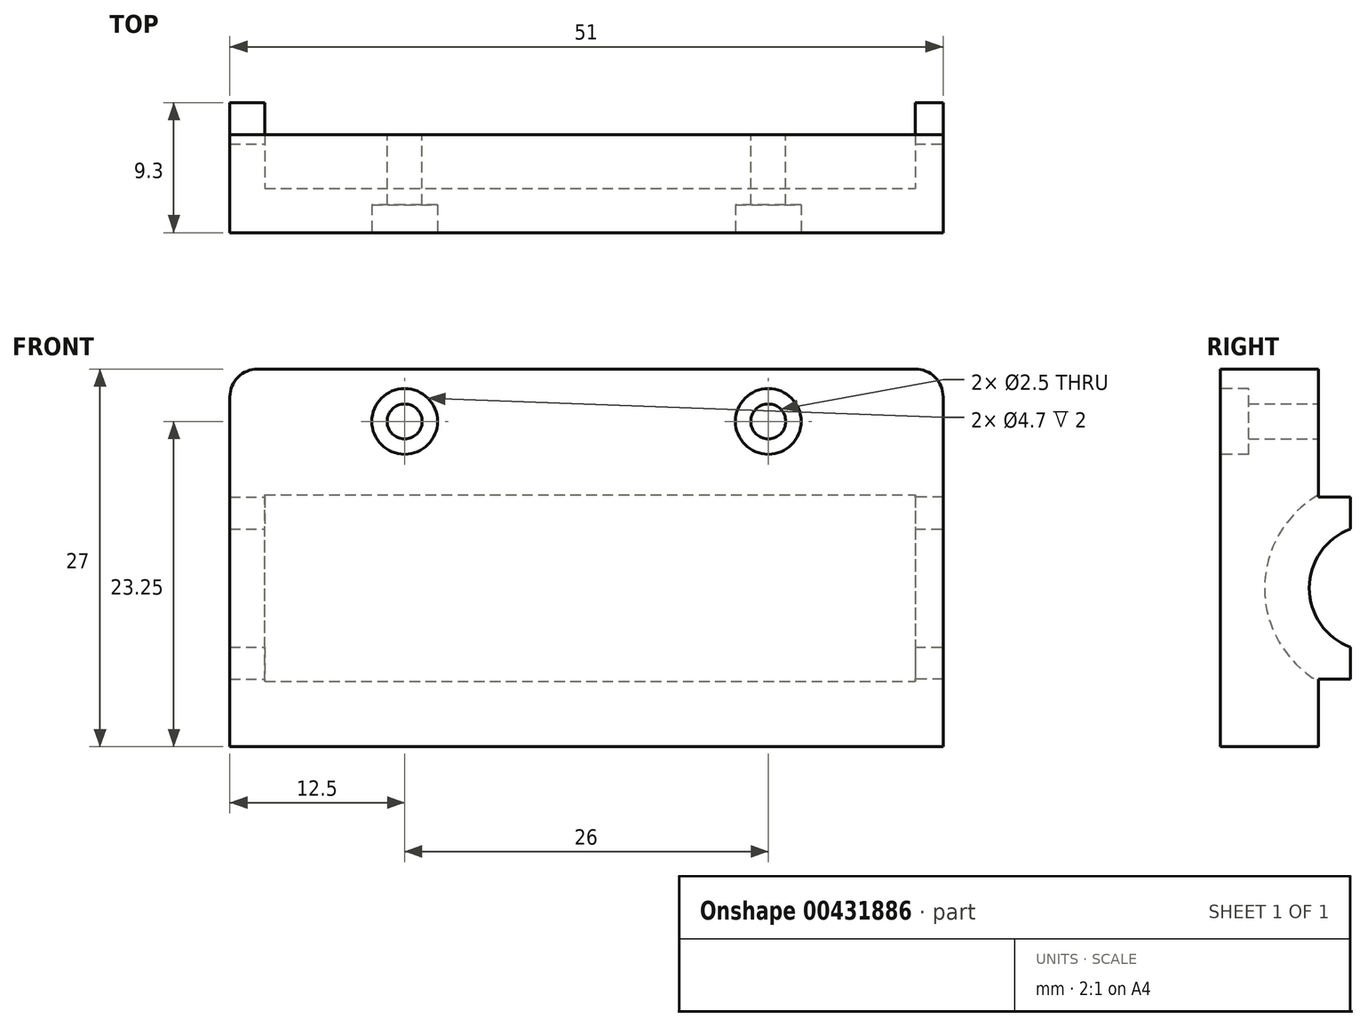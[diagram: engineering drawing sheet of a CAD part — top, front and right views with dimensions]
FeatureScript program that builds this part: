
annotation { "Feature Type Name" : "Feature", "Feature Type Description" : "" }
export const myFeature = defineFeature(function(context is Context, id is Id, definition is map)
    precondition{}
    {
        {
            var Q0;
            Q0=qCreatedBy(makeId("Front.planeOp"),FACE);
            var sketch = newSketch(context, id + "F0", { "sketchPlane" : qUnion([Q0])});
            skLineSegment(sketch, "E0.bottom", {"start": v(51, 27) * mm, "end": v(0, 27) * mm});
            skLineSegment(sketch, "E0.top", {"start": v(51, 0) * mm, "end": v(0, 0) * mm});
            skLineSegment(sketch, "E0.left", {"start": v(51, 27) * mm, "end": v(51, 0) * mm});
            skLineSegment(sketch, "E0.right", {"start": v(0, 27) * mm, "end": v(0, 0) * mm});
            skSolve(sketch);
        }
        {
            var Q0;
            Q0=makeQuery(id+"F0.imprint","IMPRINT",FACE,{"disambiguationData":[TD([[makeQuery(id+"F0.imprint","IMPRINT",EDGE,{"derivedFrom":sQuery(id+"F0.wireOp",EDGE,"E0.bottom")}),1.0]])]});
            extrude(context, id + "F1", {"entities" : qUnion([Q0]), "depth" : 7 * mm});
        }
        {
            var Q0;
            Q0=makeQuery(id+"F1.opExtrude","CAP_FACE",FACE,{"disambiguationData":[OSD([sQuery(id+"F0.wireOp",EDGE,"E0.bottom"),sQuery(id+"F0.wireOp",EDGE,"E0.top"),sQuery(id+"F0.wireOp",EDGE,"E0.left"),sQuery(id+"F0.wireOp",EDGE,"E0.right")])],"isStart":true});
            var sketch = newSketch(context, id + "F2", { "sketchPlane" : qUnion([Q0])});
            skLineSegment(sketch, "E1.bottom", {"start": v(-51, 17.83) * mm, "end": v(-48.5, 17.83) * mm});
            skLineSegment(sketch, "E1.top", {"start": v(-51, 4.83) * mm, "end": v(-48.5, 4.83) * mm});
            skLineSegment(sketch, "E1.left", {"start": v(-51, 17.83) * mm, "end": v(-51, 4.83) * mm});
            skLineSegment(sketch, "E1.right", {"start": v(-48.5, 17.83) * mm, "end": v(-48.5, 4.83) * mm});
            skLineSegment(sketch, "E2.bottom", {"start": v(0, 17.83) * mm, "end": v(-2.5, 17.83) * mm});
            skLineSegment(sketch, "E2.top", {"start": v(0, 4.83) * mm, "end": v(-2.5, 4.83) * mm});
            skLineSegment(sketch, "E2.left", {"start": v(0, 17.83) * mm, "end": v(0, 4.83) * mm});
            skLineSegment(sketch, "E2.right", {"start": v(-2.5, 17.83) * mm, "end": v(-2.5, 4.83) * mm});
            skLineSegment(sketch, "E3", {"start": v(-51, 4.83) * mm, "end": v(0, 4.83) * mm, "construction": true});
            skSolve(sketch);
        }
        {
            var Q0;
            Q0=makeQuery(id+"F2.imprint","IMPRINT",FACE,{"disambiguationData":[TD([[makeQuery(id+"F2.imprint","IMPRINT",EDGE,{"derivedFrom":sQuery(id+"F2.wireOp",EDGE,"E1.bottom")}),-1.0]])]});
            var Q1;
            Q1=makeQuery(id+"F2.imprint","IMPRINT",FACE,{"disambiguationData":[TD([[makeQuery(id+"F2.imprint","IMPRINT",EDGE,{"derivedFrom":sQuery(id+"F2.wireOp",EDGE,"E2.bottom")}),1.0]])]});
            extrude(context, id + "F3", {"entities" : qUnion([Q0, Q1]), "operationType" : NewBodyOperationType.ADD, "depth" : 2.3 * mm});
        }
        {
            var Q0;
            Q0=makeQuery(id+"F3.boolean.opBoolean","MERGE",FACE,{"derivedFrom":[makeQuery(id+"F1.opExtrude","SWEPT_FACE",FACE,{"disambiguationData":[OSD([sQuery(id+"F0.wireOp",EDGE,"E0.left")])]}),makeQuery(id+"F3.opExtrude","SWEPT_FACE",FACE,{"disambiguationData":[OSD([sQuery(id+"F2.wireOp",EDGE,"E1.left")])]})]});
            var sketch = newSketch(context, id + "F4", { "sketchPlane" : qUnion([Q0])});
            skCircle(sketch, "E4", {"center": v(3.85, 11.33) * mm, "radius": 7.55 * mm, "construction": true});
            skLineSegment(sketch, "E5", {"start": v(0, 17.83) * mm, "end": v(0, 4.83) * mm, "construction": true});
            skCircle(sketch, "E6", {"center": v(3.85, 11.33) * mm, "radius": 4.5 * mm});
            skLineSegment(sketch, "E7", {"start": v(-3.7, 21.23) * mm, "end": v(-3.7, 12.68) * mm, "construction": true});
            skLineSegment(sketch, "E8", {"start": v(3.85, 18.59) * mm, "end": v(3.85, 4.12) * mm, "construction": true});
            skLineSegment(sketch, "E9", {"start": v(2.3, 11.33) * mm, "end": v(3.85, 11.33) * mm, "construction": true});
            skSolve(sketch);
        }
        {
            var Q0;
            Q0=makeQuery(id+"F4.imprint","IMPRINT",FACE,{"disambiguationData":[TD([[makeQuery(id+"F4.imprint","IMPRINT",EDGE,{"derivedFrom":sQuery(id+"F4.wireOp",EDGE,"E6")}),1.0]])]});
            var Q1;
            Q1=makeQuery(id+"F1.opExtrude","SWEPT_BODY",BODY,{"disambiguationData":[OSD([sQuery(id+"F0.wireOp",EDGE,"E0.bottom"),sQuery(id+"F0.wireOp",EDGE,"E0.top"),sQuery(id+"F0.wireOp",EDGE,"E0.left"),sQuery(id+"F0.wireOp",EDGE,"E0.right")])]});
            extrude(context, id + "F5", {"entities" : qUnion([Q0]), "operationType" : NewBodyOperationType.REMOVE, "endBound" : BoundingType.UP_TO_BODY, "oppositeDirection" : true, "endBoundEntityBody" : qUnion([Q1]), "depth" : 35 * mm});
        }
        {
            var Q0;
            Q0=makeQuery(id+"F4.imprint","IMPRINT",FACE,{"disambiguationData":[TD([[makeQuery(id+"F4.imprint","IMPRINT",EDGE,{"derivedFrom":sQuery(id+"F4.wireOp",EDGE,"E6")}),-1.0]])]});
            cPlane(context, id + "F6", {"entities" : qUnion([Q0]), "cplaneType" : CPlaneType.OFFSET, "offset" : 2 * mm, "oppositeDirection" : true, "width" : 150 * mm, "height" : 150 * mm});
        }
        {
            var Q0;
            Q0=qCreatedBy(id+"F6.planeOp",FACE);
            var sketch = newSketch(context, id + "F7", { "sketchPlane" : qUnion([Q0])});
            skCircle(sketch, "E10", {"center": v(3.85, 11.33) * mm, "radius": 7.7 * mm});
            skSolve(sketch);
        }
        {
            var Q0;
            Q0=makeQuery(id+"F7.imprint","IMPRINT",FACE,{"disambiguationData":[TD([[makeQuery(id+"F7.imprint","IMPRINT",EDGE,{"derivedFrom":sQuery(id+"F7.wireOp",EDGE,"E10")}),1.0]])]});
            var Q1;
            {var subQ0=sQuery(id+"F2.wireOp",EDGE,"E2.right");var subQ1=sQuery(id+"F2.wireOp",EDGE,"E2.top");Q1=makeQuery(id+"F5.boolean.opBoolean","SPLIT",FACE,{"disambiguationData":[TD([makeQuery(id+"F3.opExtrude","SWEPT_FACE",FACE,{"disambiguationData":[OSD([subQ1])]})])],"derivedFrom":makeQuery(id+"F3.opExtrude","SWEPT_FACE",FACE,{"disambiguationData":[OSD([subQ0])]})});}
            extrude(context, id + "F8", {"entities" : qUnion([Q0]), "operationType" : NewBodyOperationType.REMOVE, "endBound" : BoundingType.UP_TO_SURFACE, "oppositeDirection" : true, "endBoundEntityFace" : qUnion([Q1]), "depth" : 24 * mm});
        }
        {
            var Q0;
            {var subQ3=sQuery(id+"F2.wireOp",EDGE,"E1.bottom");Q0=makeQuery(id+"F2.imprint","IMPRINT",FACE,{"disambiguationData":[TD([[makeQuery(id+"F2.imprint","IMPRINT",EDGE,{"derivedFrom":subQ3}),1.0]])]});}
            var sketch = newSketch(context, id + "F9", { "sketchPlane" : qUnion([Q0])});
            skCircle(sketch, "E11", {"center": v(-38.5, 23.25) * mm, "radius": 1.25 * mm});
            skCircle(sketch, "E12", {"center": v(-12.5, 23.25) * mm, "radius": 1.25 * mm});
            skSolve(sketch);
        }
        {
            var Q0;
            Q0=makeQuery(id+"F9.imprint","IMPRINT",FACE,{"disambiguationData":[TD([[makeQuery(id+"F9.imprint","IMPRINT",EDGE,{"derivedFrom":sQuery(id+"F9.wireOp",EDGE,"E11")}),1.0]])]});
            var Q1;
            Q1=makeQuery(id+"F9.imprint","IMPRINT",FACE,{"disambiguationData":[TD([[makeQuery(id+"F9.imprint","IMPRINT",EDGE,{"derivedFrom":sQuery(id+"F9.wireOp",EDGE,"E12")}),1.0]])]});
            extrude(context, id + "F10", {"entities" : qUnion([Q0, Q1]), "operationType" : NewBodyOperationType.REMOVE, "oppositeDirection" : true, "depth" : 25 * mm});
        }
        {
            var Q0;
            Q0=makeQuery(id+"F1.opExtrude","CAP_FACE",FACE,{"disambiguationData":[OSD([sQuery(id+"F0.wireOp",EDGE,"E0.bottom"),sQuery(id+"F0.wireOp",EDGE,"E0.top"),sQuery(id+"F0.wireOp",EDGE,"E0.left"),sQuery(id+"F0.wireOp",EDGE,"E0.right")])],"isStart":false});
            var sketch = newSketch(context, id + "F11", { "sketchPlane" : qUnion([Q0])});
            skCircle(sketch, "E13", {"center": v(12.5, 23.25) * mm, "radius": 2.35 * mm});
            skCircle(sketch, "E14", {"center": v(38.5, 23.25) * mm, "radius": 2.35 * mm});
            skSolve(sketch);
        }
        {
            var Q0;
            Q0=makeQuery(id+"F11.imprint","IMPRINT",FACE,{"disambiguationData":[TD([[makeQuery(id+"F11.imprint","IMPRINT",EDGE,{"derivedFrom":sQuery(id+"F11.wireOp",EDGE,"E13")}),1.0]])]});
            var Q1;
            Q1=makeQuery(id+"F11.imprint","IMPRINT",FACE,{"disambiguationData":[TD([[makeQuery(id+"F11.imprint","IMPRINT",EDGE,{"derivedFrom":sQuery(id+"F11.wireOp",EDGE,"E14")}),1.0]])]});
            extrude(context, id + "F12", {"entities" : qUnion([Q0, Q1]), "operationType" : NewBodyOperationType.REMOVE, "oppositeDirection" : true, "depth" : 2 * mm});
        }
        {
            var Q0;
            Q0=makeQuery(id+"F1.opExtrude","SWEPT_EDGE",EDGE,{"disambiguationData":[OSD([sQuery(id+"F0.wireOp",EDGE,"E0.bottom"),sQuery(id+"F0.wireOp",EDGE,"E0.right")])]});
            var Q1;
            Q1=makeQuery(id+"F1.opExtrude","SWEPT_EDGE",EDGE,{"disambiguationData":[OSD([sQuery(id+"F0.wireOp",EDGE,"E0.bottom"),sQuery(id+"F0.wireOp",EDGE,"E0.left")])]});
            fillet(context, id + "F13", {"entities" : qUnion([Q0, Q1]), "radius" : 2 * mm, "tangentPropagation" : true, "allowEdgeOverflow" : false});
        }
    });
